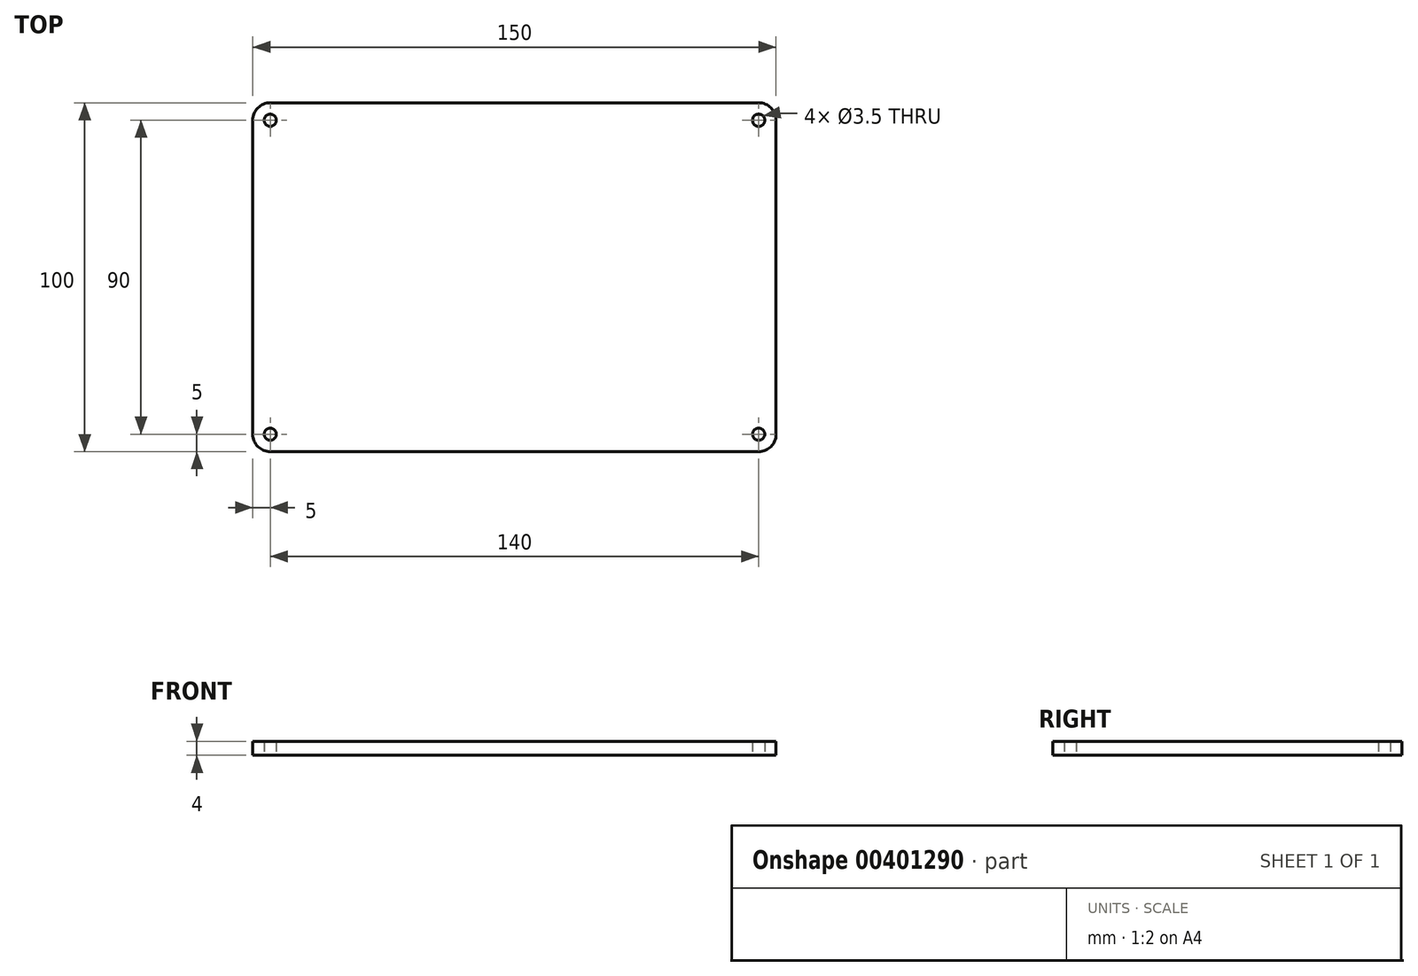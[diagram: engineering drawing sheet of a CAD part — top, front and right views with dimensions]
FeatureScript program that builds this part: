
annotation { "Feature Type Name" : "Feature", "Feature Type Description" : "" }
export const myFeature = defineFeature(function(context is Context, id is Id, definition is map)
    precondition{}
    {
        {
            var Q0;
            Q0=qCreatedBy(makeId("Top.planeOp"),FACE);
            var sketch = newSketch(context, id + "F0", { "sketchPlane" : qUnion([Q0])});
            skLineSegment(sketch, "E0.bottom", {"start": v(-75, 50) * mm, "end": v(75, 50) * mm});
            skLineSegment(sketch, "E0.top", {"start": v(-75, -50) * mm, "end": v(75, -50) * mm});
            skLineSegment(sketch, "E0.left", {"start": v(-75, 50) * mm, "end": v(-75, -50) * mm});
            skLineSegment(sketch, "E0.right", {"start": v(75, 50) * mm, "end": v(75, -50) * mm});
            skPoint(sketch, "E0.middle", {"position": v(0, 0) * mm});
            skCircle(sketch, "E1", {"center": v(-70, 45) * mm, "radius": 1.75 * mm});
            skCircle(sketch, "E2.MirrorC", {"center": v(70, 45) * mm, "radius": 1.75 * mm});
            skCircle(sketch, "E3.MirrorC", {"center": v(-70, -45) * mm, "radius": 1.75 * mm});
            skCircle(sketch, "E4.MirrorC", {"center": v(70, -45) * mm, "radius": 1.75 * mm});
            skSolve(sketch);
        }
        {
            var Q0;
            Q0 = qSketchRegion(id + "F0", true);
            extrude(context, id + "F1", {"entities" : qUnion([Q0]), "depth" : 4 * mm, "offsetDistance" : 25 * mm});
        }
        {
            var Q0;
            Q0=makeQuery(id+"F1.opExtrude","SWEPT_EDGE",EDGE,{"disambiguationData":[OSD([sQuery(id+"F0.wireOp",EDGE,"E0.bottom"),sQuery(id+"F0.wireOp",EDGE,"E0.left")])]});
            var Q1;
            Q1=makeQuery(id+"F1.opExtrude","SWEPT_EDGE",EDGE,{"disambiguationData":[OSD([sQuery(id+"F0.wireOp",EDGE,"E0.bottom"),sQuery(id+"F0.wireOp",EDGE,"E0.right")])]});
            var Q2;
            Q2=makeQuery(id+"F1.opExtrude","SWEPT_EDGE",EDGE,{"disambiguationData":[OSD([sQuery(id+"F0.wireOp",EDGE,"E0.top"),sQuery(id+"F0.wireOp",EDGE,"E0.right")])]});
            var Q3;
            Q3=makeQuery(id+"F1.opExtrude","SWEPT_EDGE",EDGE,{"disambiguationData":[OSD([sQuery(id+"F0.wireOp",EDGE,"E0.top"),sQuery(id+"F0.wireOp",EDGE,"E0.left")])]});
            fillet(context, id + "F2", {"entities" : qUnion([Q0, Q1, Q2, Q3]), "radius" : 5 * mm, "tangentPropagation" : true, "allowEdgeOverflow" : false});
        }
    });
